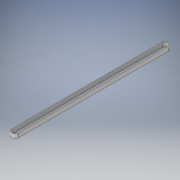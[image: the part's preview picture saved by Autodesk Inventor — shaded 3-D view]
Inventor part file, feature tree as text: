
AUTODESK INVENTOR PART (.ipt)
format: ipt  version: 2019 (Build 230136000, 136)  size: 106,496 bytes
history: native  units: mm
features: extrude x1, sketch x1
ambient origin geometry x8: Origin, YZ Plane, XZ Plane, XY Plane, X Axis, Y Axis, Z Axis, Center Point
bodies: Solid1 (feature_tree)
feature tree (2):
  extrude  "Extrusion1"  Depth=15.0mm
  sketch  "Sketch1"  dims[d0=10.0mm d1=546.0mm d2=3.0mm d3=15.0mm d4=0.0mm]
